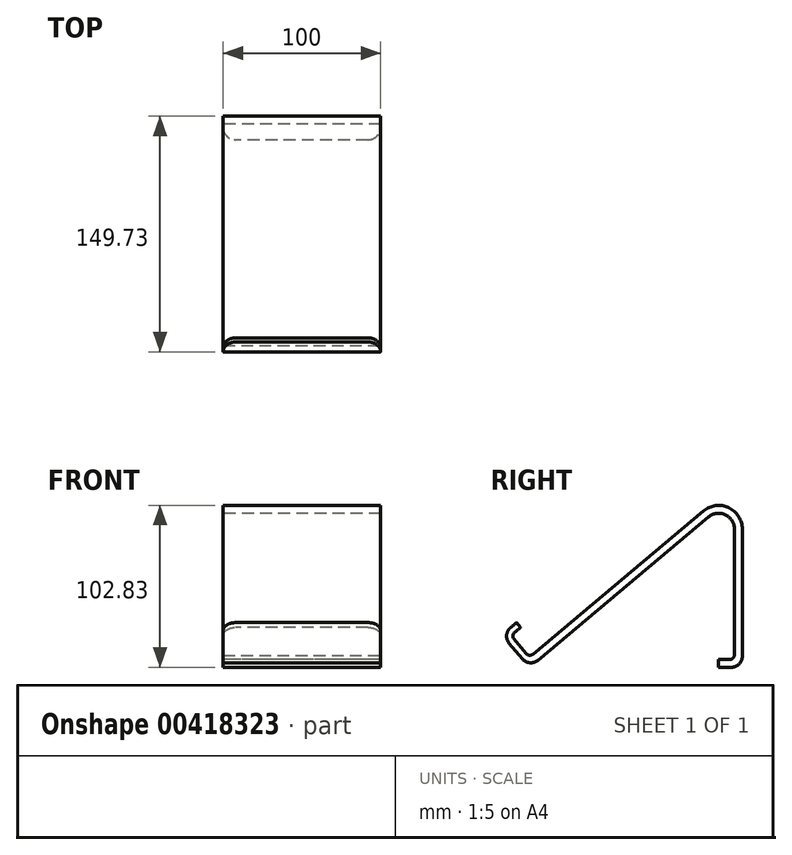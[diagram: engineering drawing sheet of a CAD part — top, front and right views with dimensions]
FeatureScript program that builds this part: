
annotation { "Feature Type Name" : "Feature", "Feature Type Description" : "" }
export const myFeature = defineFeature(function(context is Context, id is Id, definition is map)
    precondition{}
    {
        {
            var Q0;
            Q0=qCreatedBy(makeId("Right.planeOp"),FACE);
            var sketch = newSketch(context, id + "F0", { "sketchPlane" : qUnion([Q0])});
            skLineSegment(sketch, "E0", {"start": v(-135.23, 0) * mm, "end": v(-152.59, 20.68) * mm});
            skLineSegment(sketch, "E1", {"start": v(-152.59, 20.68) * mm, "end": v(-143.4, 28.4) * mm});
            skLineSegment(sketch, "E2", {"start": v(-143.4, 28.4) * mm, "end": v(-140.82, 25.33) * mm});
            skLineSegment(sketch, "E3", {"start": v(-140.82, 25.33) * mm, "end": v(-146.95, 20.2) * mm});
            skLineSegment(sketch, "E4", {"start": v(-146.95, 20.2) * mm, "end": v(-135.38, 6.4) * mm});
            skLineSegment(sketch, "E5", {"start": v(-135.38, 6.4) * mm, "end": v(-24.64, 99.32) * mm});
            skLineSegment(sketch, "E6", {"start": v(0, 87.83) * mm, "end": v(0, 0) * mm});
            skLineSegment(sketch, "E7", {"start": v(0, 0) * mm, "end": v(-15, 0) * mm});
            skLineSegment(sketch, "E8", {"start": v(-15, 0) * mm, "end": v(-15, 5) * mm});
            skLineSegment(sketch, "E9", {"start": v(-135.23, 0) * mm, "end": v(-21.43, 95.5) * mm});
            skLineSegment(sketch, "E10", {"start": v(-5, 87.83) * mm, "end": v(-5, 5) * mm});
            skLineSegment(sketch, "E11", {"start": v(-5, 5) * mm, "end": v(-15, 5) * mm});
            skPoint(sketch, "E12.visualSharp", {"position": v(-5, 109.28) * mm});
            skArc(sketch, "E12.filletArc", {"start": v(-5, 87.83) * mm, "mid": v(-10.77, 96.9) * mm, "end": v(-21.43, 95.5) * mm});
            skPoint(sketch, "E13.visualSharp", {"position": v(0, 120) * mm});
            skArc(sketch, "E13.filletArc", {"start": v(0, 87.83) * mm, "mid": v(-8.66, 101.43) * mm, "end": v(-24.64, 99.32) * mm});
            skSolve(sketch);
        }
        {
            var Q0;
            Q0=qSketchRegion(id+"F0",true);
            extrude(context, id + "F1", {"entities" : qUnion([Q0]), "endBound" : BoundingType.SYMMETRIC, "depth" : 100 * mm, "offsetDistance" : 25 * mm});
        }
        {
            var Q0;
            Q0=makeQuery(id+"F1.opExtrude","SWEPT_EDGE",EDGE,{"disambiguationData":[OSD([sQuery(id+"F0.wireOp",EDGE,"E0"),sQuery(id+"F0.wireOp",EDGE,"E9")])]});
            var Q1;
            Q1=makeQuery(id+"F1.opExtrude","SWEPT_EDGE",EDGE,{"disambiguationData":[OSD([sQuery(id+"F0.wireOp",EDGE,"E0"),sQuery(id+"F0.wireOp",EDGE,"E1")])]});
            var Q2;
            Q2=makeQuery(id+"F1.opExtrude","SWEPT_EDGE",EDGE,{"disambiguationData":[OSD([sQuery(id+"F0.wireOp",EDGE,"E6"),sQuery(id+"F0.wireOp",EDGE,"E7")])]});
            fillet(context, id + "F2", {"entities" : qUnion([Q0, Q1, Q2]), "radius" : 7 * mm, "tangentPropagation" : true, "allowEdgeOverflow" : false});
        }
        {
            var Q0;
            Q0=makeQuery(id+"F1.opExtrude","SWEPT_EDGE",EDGE,{"disambiguationData":[OSD([sQuery(id+"F0.wireOp",EDGE,"E3"),sQuery(id+"F0.wireOp",EDGE,"E4")])]});
            var Q1;
            Q1=makeQuery(id+"F1.opExtrude","SWEPT_EDGE",EDGE,{"disambiguationData":[OSD([sQuery(id+"F0.wireOp",EDGE,"E4"),sQuery(id+"F0.wireOp",EDGE,"E5")])]});
            var Q2;
            Q2=makeQuery(id+"F1.opExtrude","SWEPT_EDGE",EDGE,{"disambiguationData":[OSD([sQuery(id+"F0.wireOp",EDGE,"E10"),sQuery(id+"F0.wireOp",EDGE,"E11")])]});
            fillet(context, id + "F3", {"entities" : qUnion([Q0, Q1, Q2]), "radius" : 3 * mm, "tangentPropagation" : true, "allowEdgeOverflow" : false});
        }
        {
            var Q0;
            Q0=makeQuery(id+"F1.opExtrude","CAP_EDGE",EDGE,{"disambiguationData":[OSD([sQuery(id+"F0.wireOp",EDGE,"E2")])],"isStart":false});
            var Q1;
            Q1=makeQuery(id+"F1.opExtrude","CAP_EDGE",EDGE,{"disambiguationData":[OSD([sQuery(id+"F0.wireOp",EDGE,"E2")])],"isStart":true});
            var Q2;
            Q2=makeQuery(id+"F1.opExtrude","CAP_EDGE",EDGE,{"disambiguationData":[OSD([sQuery(id+"F0.wireOp",EDGE,"E8")])],"isStart":false});
            var Q3;
            Q3=makeQuery(id+"F1.opExtrude","CAP_EDGE",EDGE,{"disambiguationData":[OSD([sQuery(id+"F0.wireOp",EDGE,"E8")])],"isStart":true});
            fillet(context, id + "F4", {"entities" : qUnion([Q0, Q1, Q2, Q3]), "radius" : 8 * mm, "tangentPropagation" : true, "allowEdgeOverflow" : false});
        }
    });
